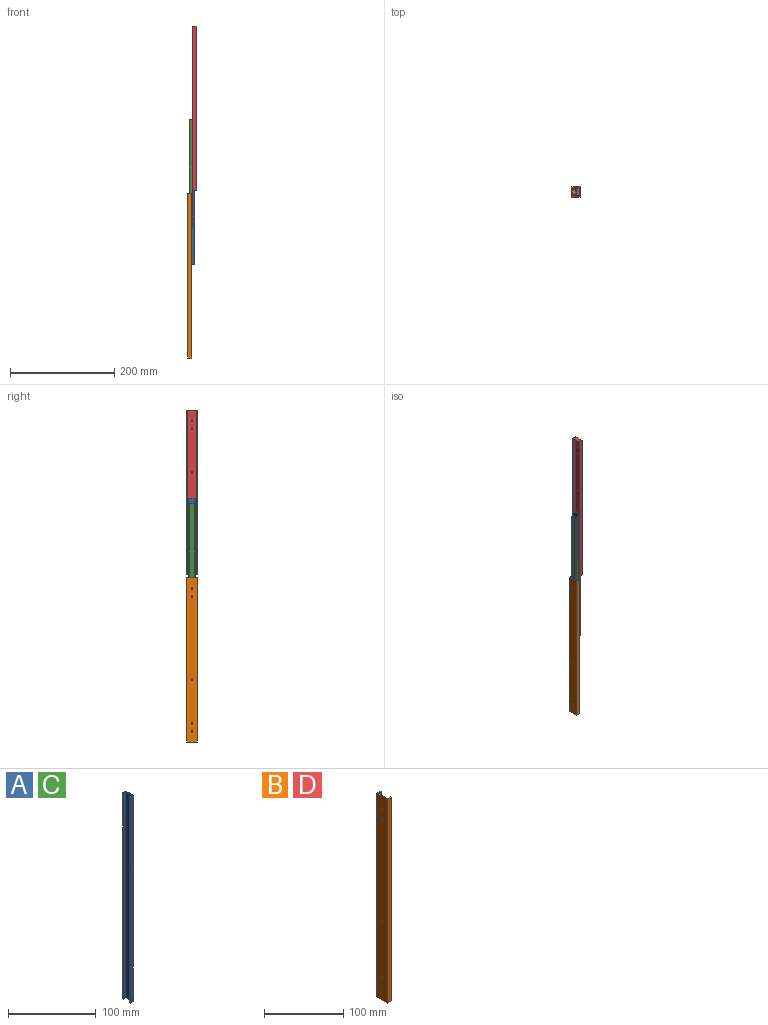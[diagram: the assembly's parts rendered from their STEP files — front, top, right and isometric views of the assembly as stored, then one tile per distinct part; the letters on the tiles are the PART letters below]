
ASSEMBLY  parts=4 mates=3
PART A: 10 faces, bbox 5.2x12x287 mm
  f0: plane 287x12mm, normal (1,0,0), area 3444mm2, adj f1,f7,f8,f9
  f1: plane 287x5.2mm, normal (0,1,0), area 1492.4mm2, adj f0,f6,f8,f9
  f2: plane 287x1.27mm, normal (-1,0,0), area 364.5mm2, adj f3,f7,f8,f9
  f3: plane 287x3.93mm, normal (0,1,0), area 1127.9mm2, adj f2,f4,f8,f9
  f4: plane 287x9.46mm, normal (-1,0,0), area 2715mm2, adj f3,f5,f8,f9
  f5: plane 287x3.93mm, normal (0,-1,0), area 1127.9mm2, adj f4,f6,f8,f9
  f6: plane 287x1.27mm, normal (-1,0,0), area 364.5mm2, adj f1,f5,f8,f9
  f7: plane 287x5.2mm, normal (0,-1,0), area 1492.4mm2, adj f0,f2,f8,f9
  f8: plane 12x5.2mm, normal (0,0,-1), area 25.2mm2, adj f0,f1,f2,f3,f4,f5,f6,f7
  f9: plane 12x5.2mm, normal (0,0,1), area 25.2mm2, adj f0,f1,f2,f3,f4,f5,f6,f7
PART B: 28 faces, bbox 7x20x315 mm
  f0: plane 315x7mm, normal (0,-1,0), area 2205mm2, adj f5,f6,f25,f27
  f1: plane 315x16.96mm, normal (1,0,0), area 5273.2mm2, adj f3,f4,f7,f8,f9,f10,f11,f12
  f2: plane 315x1.52mm, normal (1,0,0), area 478.8mm2, adj f3,f24,f25,f27
  f3: plane 315x5.48mm, normal (0,-1,0), area 1726.2mm2, adj f1,f2,f25,f27
  f4: plane 315x5.48mm, normal (0,1,0), area 1726.2mm2, adj f1,f5,f25,f27
  f5: plane 315x1.52mm, normal (1,0,0), area 478.8mm2, adj f0,f4,f25,f27
  f6: plane 315x20mm, normal (-1,0,0), area 6252.1mm2, adj f0,f7,f8,f9,f10,f11,f12,f13
  f7: cylinder r=1.6mm len=3.2mm, axis (-1,0,0), area 15.3mm2, adj f1,f6
  f8: plane 1.52x0.8mm, normal (0,1,0), area 1.2mm2, adj f1,f6,f9,f11
  f9: cylinder r=1.6mm len=3.2mm, axis (-1,0,0), area 7.6mm2, adj f1,f6,f8,f10
  f10: plane 1.52x0.8mm, normal (0,-1,0), area 1.2mm2, adj f1,f6,f9,f11
  f11: cylinder r=1.6mm len=3.2mm, axis (-1,0,0), area 7.6mm2, adj f1,f6,f8,f10
  f12: plane 1.52x0.8mm, normal (0,1,0), area 1.2mm2, adj f1,f6,f13,f15
  f13: cylinder r=1.6mm len=3.2mm, axis (-1,0,0), area 7.6mm2, adj f1,f6,f12,f14
  f14: plane 1.52x0.8mm, normal (0,-1,0), area 1.2mm2, adj f1,f6,f13,f15
  f15: cylinder r=1.6mm len=3.2mm, axis (-1,0,0), area 7.6mm2, adj f1,f6,f12,f14
  f16: plane 1.52x0.8mm, normal (0,1,0), area 1.2mm2, adj f1,f6,f17,f19
  f17: cylinder r=1.6mm len=3.2mm, axis (-1,0,0), area 7.6mm2, adj f1,f6,f16,f18
  f18: plane 1.52x0.8mm, normal (0,-1,0), area 1.2mm2, adj f1,f6,f17,f19
  f19: cylinder r=1.6mm len=3.2mm, axis (-1,0,0), area 7.6mm2, adj f1,f6,f16,f18
  f20: plane 5x1.52mm, normal (0,-1,0), area 7.6mm2, adj f1,f21,f23,f25
  f21: plane 14x5mm, normal (0,0,1), area 70mm2, adj f1,f20,f22,f23
  f22: plane 5x1.52mm, normal (0,1,0), area 7.6mm2, adj f1,f21,f23,f25
  f23: plane 14x1.52mm, normal (1,0,0), area 21.3mm2, adj f20,f21,f22,f25
  f24: plane 315x7mm, normal (0,1,0), area 2205mm2, adj f2,f6,f25,f27
  f25: plane 20x7mm, normal (0,0,-1), area 117.1mm2, adj f0,f1,f2,f3,f4,f5,f6,f20
  f26: cylinder r=1.6mm len=3.2mm, axis (-1,0,0), area 15.3mm2, adj f1,f6
  f27: plane 20x7mm, normal (0,0,1), area 47.1mm2, adj f0,f1,f2,f3,f4,f5,f6,f24
PART C: same geometry as A
PART D: same geometry as B
PLACE A rot(axis=(0,0,-1),180deg) t=(134.47,-48.82,-181.99)mm
PLACE B t=(127.58,-48.82,-361.99)mm
PLACE C rot(axis=(1,0,0),180deg) t=(129.27,-48.82,95.01)mm
PLACE D rot(axis=(0,-1,0),180deg) t=(136.16,-48.82,275.01)mm
MATE fastened C.f0 <-> A.f0  axis (1,0,0) through (131.87,-48.82,-48.49)mm
MATE slider B.f25 <-> C.f9  axis (0,0,-1) through (130.6,-48.82,-361.99)mm
MATE slider D.f25 <-> A.f9  axis (0,0,1) through (133.14,-48.82,275.01)mm
